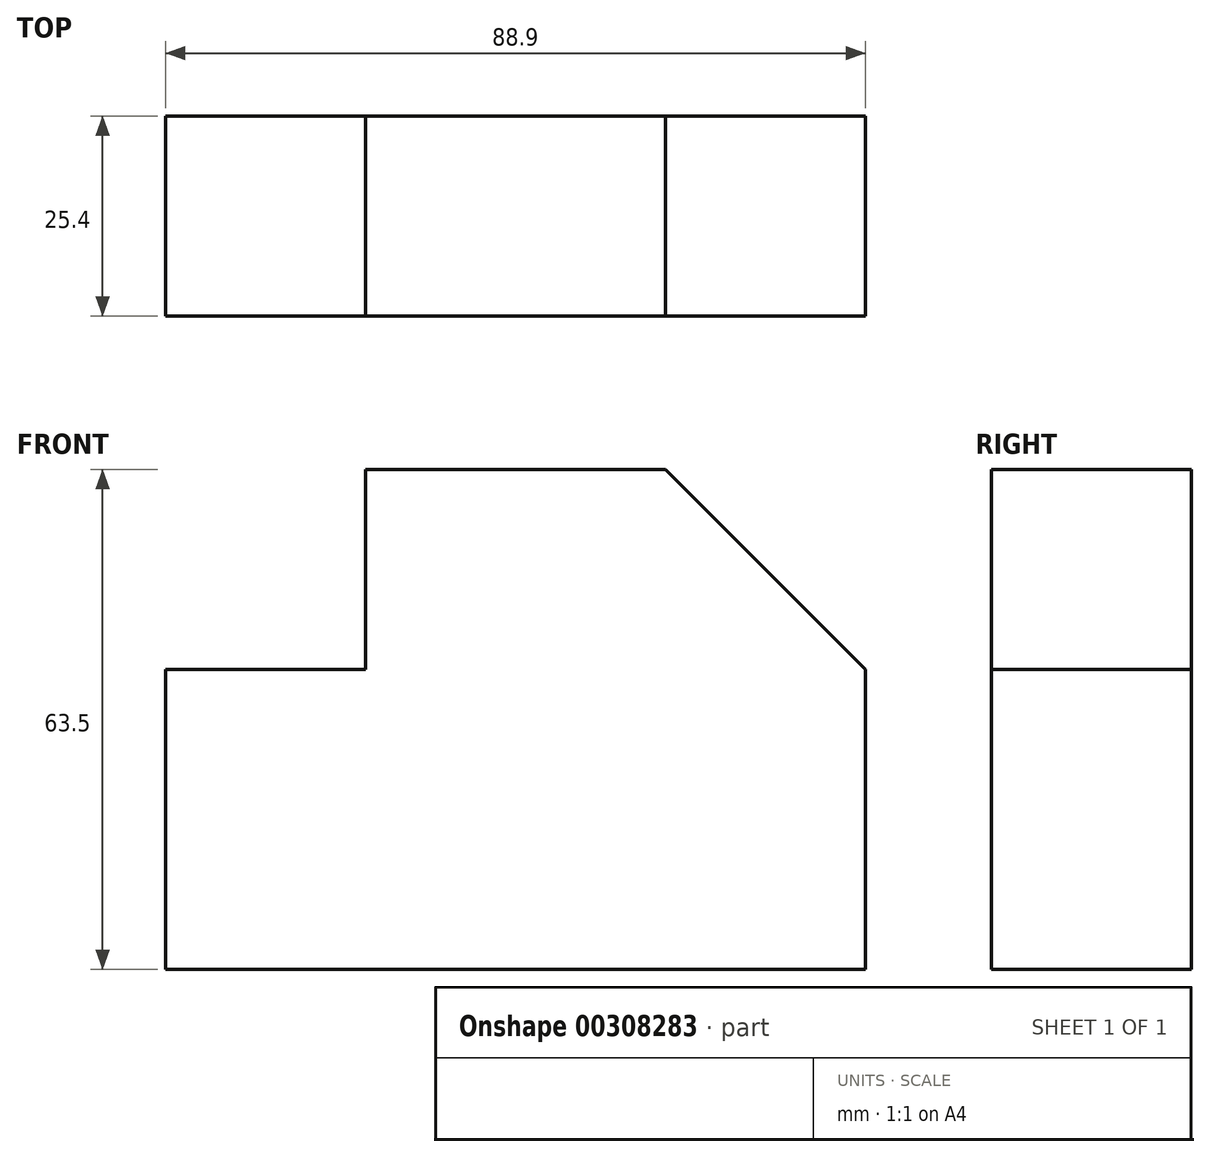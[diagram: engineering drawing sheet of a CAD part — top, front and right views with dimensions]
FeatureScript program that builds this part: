
annotation { "Feature Type Name" : "Feature", "Feature Type Description" : "" }
export const myFeature = defineFeature(function(context is Context, id is Id, definition is map)
    precondition{}
    {
        {
            var Q0;
            Q0=qCreatedBy(makeId("Front.planeOp"),FACE);
            var sketch = newSketch(context, id + "F0", { "sketchPlane" : qUnion([Q0])});
            skLineSegment(sketch, "E0", {"start": v(-49.73, -38.1) * mm, "end": v(39.17, -38.1) * mm});
            skLineSegment(sketch, "E1", {"start": v(39.17, -38.1) * mm, "end": v(39.17, 0) * mm});
            skLineSegment(sketch, "E2", {"start": v(39.17, 0) * mm, "end": v(13.77, 25.4) * mm});
            skLineSegment(sketch, "E3", {"start": v(13.77, 25.4) * mm, "end": v(-24.33, 25.4) * mm});
            skLineSegment(sketch, "E4", {"start": v(-24.33, 25.4) * mm, "end": v(-24.33, 0) * mm});
            skLineSegment(sketch, "E5", {"start": v(-24.33, 0) * mm, "end": v(-49.73, 0) * mm});
            skLineSegment(sketch, "E6", {"start": v(-49.73, 0) * mm, "end": v(-49.73, -38.1) * mm});
            skSolve(sketch);
        }
        {
            var Q0;
            Q0=makeQuery(id+"F0.imprint","IMPRINT",FACE,{"disambiguationData":[TD([[makeQuery(id+"F0.imprint","IMPRINT",EDGE,{"derivedFrom":sQuery(id+"F0.wireOp",EDGE,"E0")}),1.0]])]});
            extrude(context, id + "F1", {"entities" : qUnion([Q0]), "depth" : 25.4 * mm});
        }
    });
